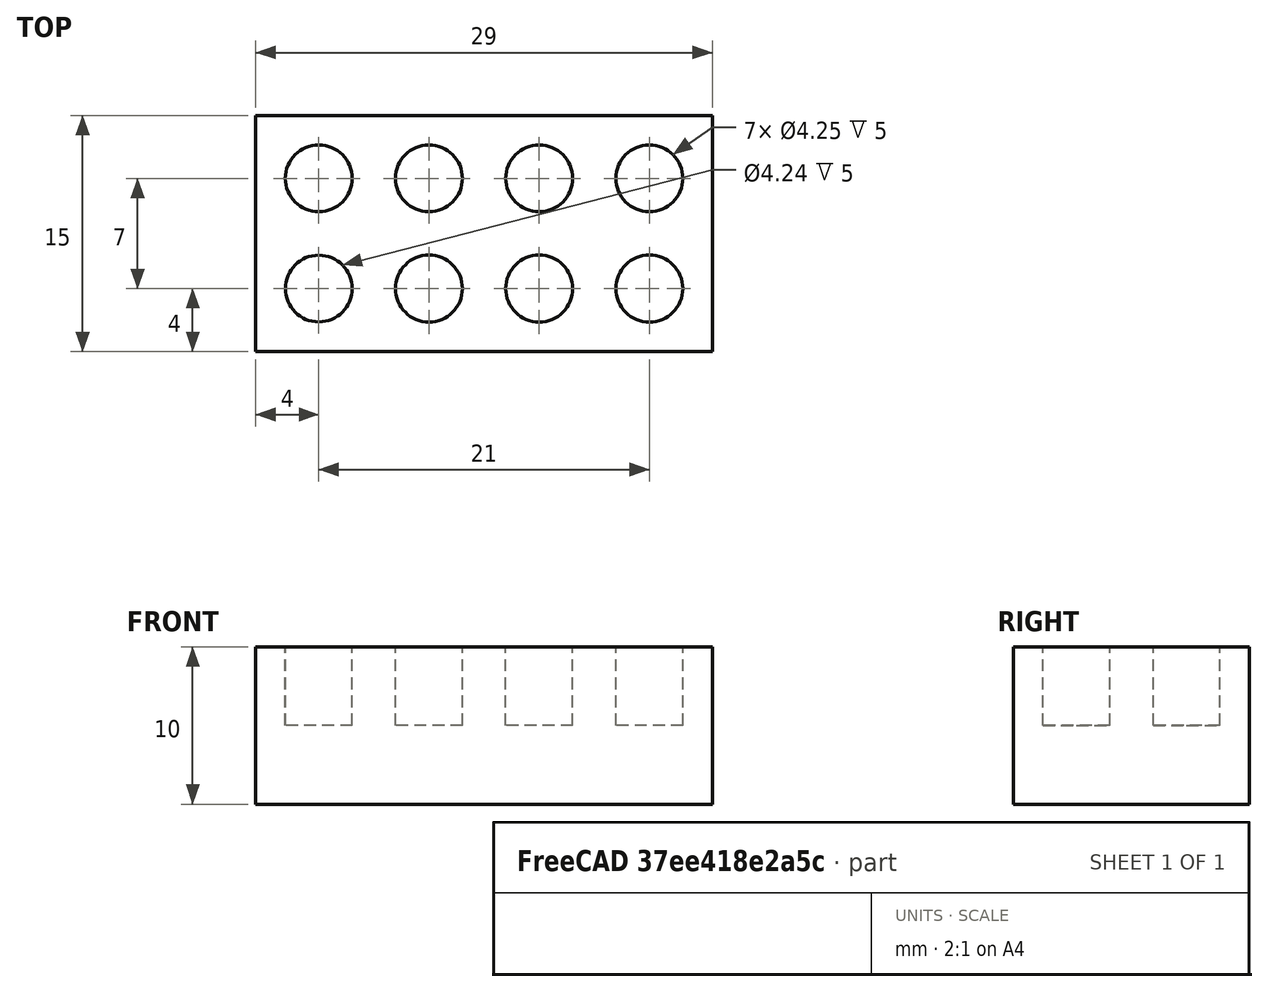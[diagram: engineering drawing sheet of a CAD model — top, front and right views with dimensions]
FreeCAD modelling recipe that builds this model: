
FCSTD DOCUMENT  (FreeCAD 0.19R24276 (Git))
Label: Test Piece 0.1
License: All rights reserved
LicenseURL: http://en.wikipedia.org/wiki/All_rights_reserved
objects: Part::Cylinder×8, Part::Box×1, Part::MultiFuse×1, Part::Cut×1
note: 11 computed .brp shape members not serialized (recipe doc carries the construction recipe); baked Part::Feature solids carry a one-line shape summary decoded from their .brp

FEATURE [Part::Box] Box  label="Cube"
  AttacherType = Attacher::AttachEngine3D
  Height = 10
  Length = 29
  Width = 15
FEATURE [Part::Cylinder] Cylinder
  Angle = 360
  AttacherType = Attacher::AttachEngine3D
  Height = 5
  Placement = pos=(4,4,5) rot=(0,0,1;0rad)
  Radius = 2.12
FEATURE [Part::Cylinder] Cylinder001
  Angle = 360
  AttacherType = Attacher::AttachEngine3D
  Height = 5
  Placement = pos=(11,4,5) rot=(0,0,1;0rad)
  Radius = 2.125
FEATURE [Part::Cylinder] Cylinder002
  Angle = 360
  AttacherType = Attacher::AttachEngine3D
  Height = 5
  Placement = pos=(11,11,5) rot=(0,0,1;0rad)
  Radius = 2.125
FEATURE [Part::Cylinder] Cylinder003
  Angle = 360
  AttacherType = Attacher::AttachEngine3D
  Height = 5
  Placement = pos=(4,11,5) rot=(0,0,1;0rad)
  Radius = 2.125
FEATURE [Part::Cylinder] Cylinder004
  Angle = 360
  AttacherType = Attacher::AttachEngine3D
  Height = 5
  Placement = pos=(18,11,5) rot=(0,0,1;0rad)
  Radius = 2.125
FEATURE [Part::Cylinder] Cylinder005
  Angle = 360
  AttacherType = Attacher::AttachEngine3D
  Height = 5
  Placement = pos=(25,4,5) rot=(0,0,1;0rad)
  Radius = 2.125
FEATURE [Part::Cylinder] Cylinder006
  Angle = 360
  AttacherType = Attacher::AttachEngine3D
  Height = 5
  Placement = pos=(18,4,5) rot=(0,0,1;0rad)
  Radius = 2.125
FEATURE [Part::Cylinder] Cylinder007
  Angle = 360
  AttacherType = Attacher::AttachEngine3D
  Height = 5
  Placement = pos=(25,11,5) rot=(0,0,1;0rad)
  Radius = 2.125
FEATURE [Part::MultiFuse] Fusion
  Shapes = -> [Cylinder,Cylinder003,Cylinder005,Cylinder004,Cylinder002,Cylinder001,Cylinder006,Cylinder007]
FEATURE [Part::Cut] Cut  label="Holes good size on Ultimaker. Too big (correct size) on Fisher"
  Base = -> Box
  Tool = -> Fusion
